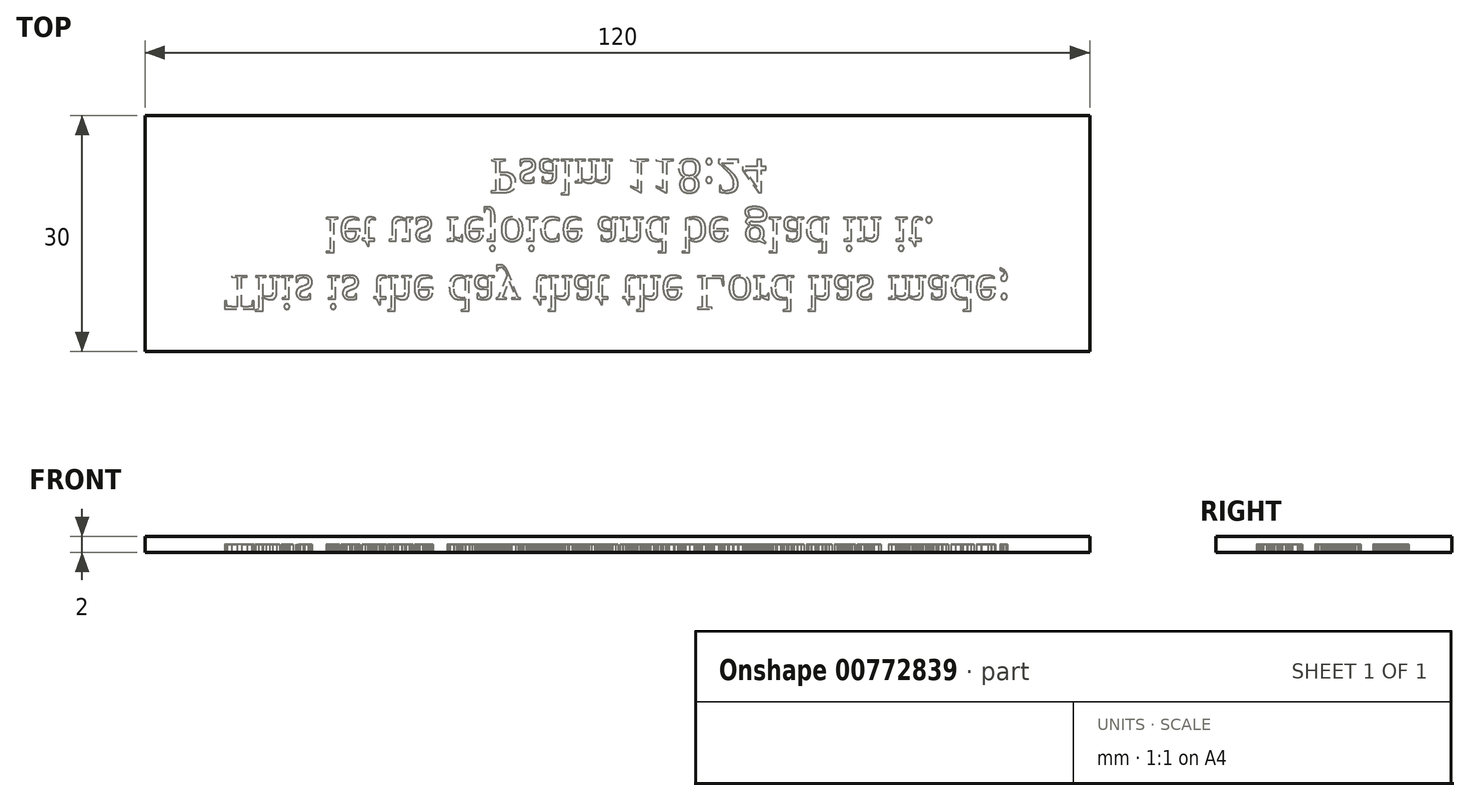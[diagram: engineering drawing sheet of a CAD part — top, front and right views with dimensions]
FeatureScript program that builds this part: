
annotation { "Feature Type Name" : "Feature", "Feature Type Description" : "" }
export const myFeature = defineFeature(function(context is Context, id is Id, definition is map)
    precondition{}
    {
        {
            var Q0;
            Q0=qCreatedBy(makeId("Top.planeOp"),FACE);
            var sketch = newSketch(context, id + "F0", { "sketchPlane" : qUnion([Q0])});
            skLineSegment(sketch, "E0.bottom", {"start": v(-23.08, -1.26) * mm, "end": v(96.92, -1.26) * mm});
            skLineSegment(sketch, "E0.top", {"start": v(-23.08, -31.26) * mm, "end": v(96.92, -31.26) * mm});
            skLineSegment(sketch, "E0.left", {"start": v(-23.08, -1.26) * mm, "end": v(-23.08, -31.26) * mm});
            skLineSegment(sketch, "E0.right", {"start": v(96.92, -1.26) * mm, "end": v(96.92, -31.26) * mm});
            skSolve(sketch);
        }
        {
            var Q0;
            Q0 = qSketchRegion(id + "F0", true);
            extrude(context, id + "F1", {"entities" : qUnion([Q0]), "depth" : 2 * mm, "offsetDistance" : 25 * mm});
        }
        {
            var Q0;
            Q0=makeQuery(id+"F1.opExtrude","CAP_FACE",FACE,{"disambiguationData":[OSD([sQuery(id+"F0.wireOp",EDGE,"E0.bottom"),sQuery(id+"F0.wireOp",EDGE,"E0.top"),sQuery(id+"F0.wireOp",EDGE,"E0.left"),sQuery(id+"F0.wireOp",EDGE,"E0.right")])],"isStart":true});
            var sketch = newSketch(context, id + "F2", { "sketchPlane" : qUnion([Q0])});
            skText(sketch, "E1", { "text": "This is the day that the Lord has made;\n        let us rejoice and be glad in it. \n                     Psalm 118:24", "fontName": "Tinos-Regular.ttf"});
            const initialGuessF2  = {"E1": [-0.01308, 0.02162, 1, 0, 0.00463]};
            skSetInitialGuess(sketch, initialGuessF2);
            skSolve(sketch);
        }
        {
            var Q0;
            Q0 = qSketchRegion(id + "F2", true);
            extrude(context, id + "F3", {"entities" : qUnion([Q0]), "operationType" : NewBodyOperationType.REMOVE, "oppositeDirection" : true, "depth" : 1 * mm, "offsetDistance" : 25 * mm});
        }
    });
